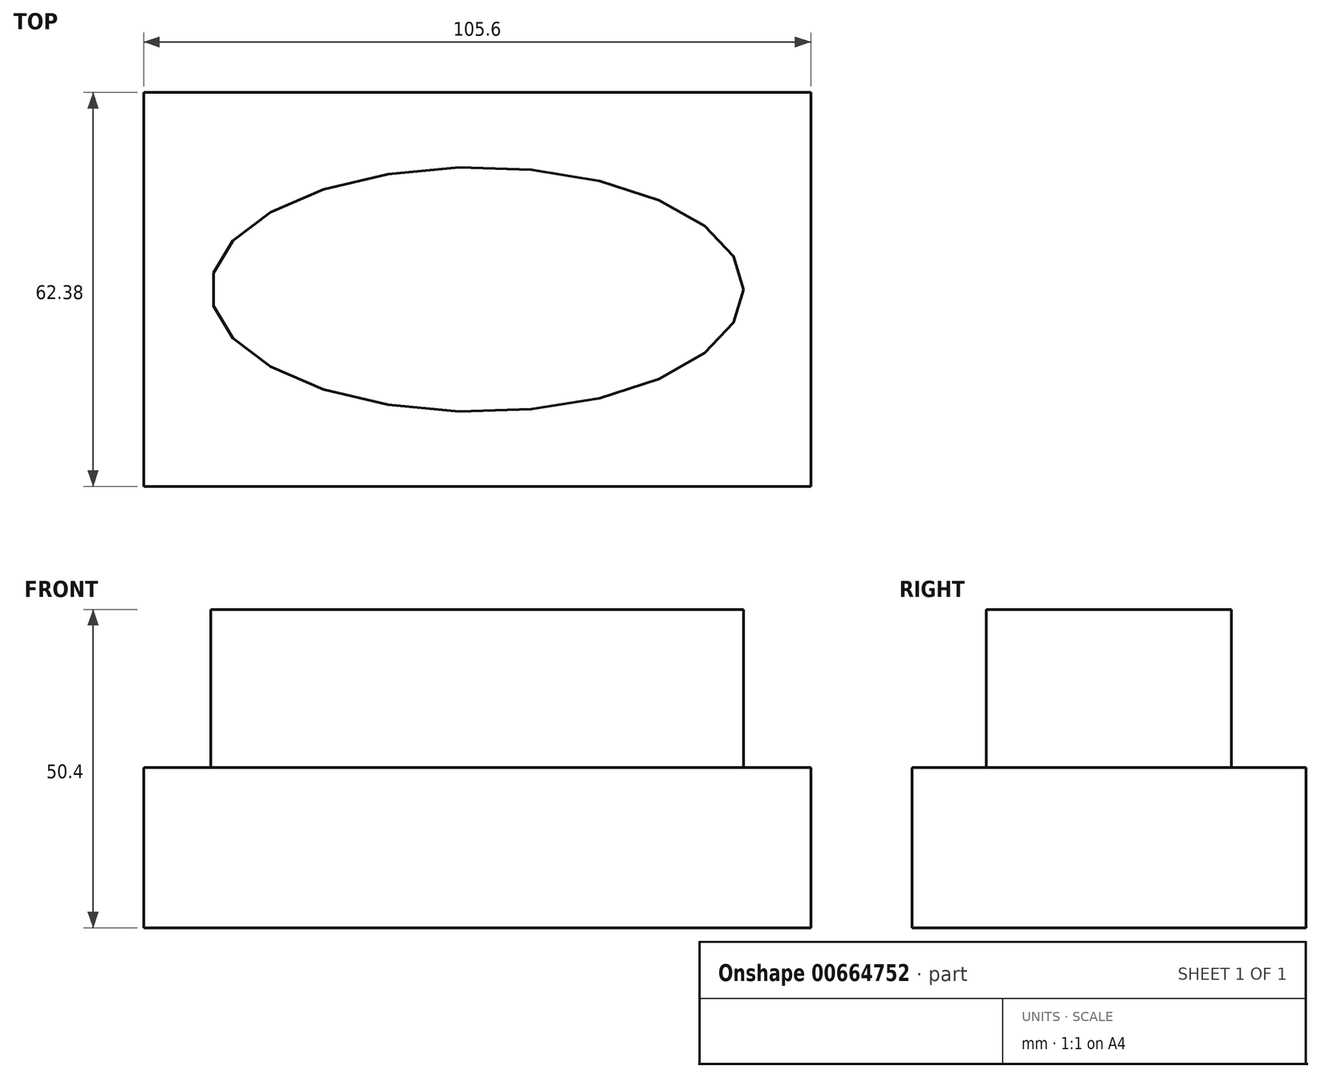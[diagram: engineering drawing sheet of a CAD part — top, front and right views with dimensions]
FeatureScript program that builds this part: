
annotation { "Feature Type Name" : "Feature", "Feature Type Description" : "" }
export const myFeature = defineFeature(function(context is Context, id is Id, definition is map)
    precondition{}
    {
        {
            var Q0;
            Q0=qCreatedBy(makeId("Top.planeOp"),FACE);
            var sketch = newSketch(context, id + "F0", { "sketchPlane" : qUnion([Q0])});
            skLineSegment(sketch, "E0.bottom", {"start": v(52.8, 31.19) * mm, "end": v(-52.8, 31.19) * mm});
            skLineSegment(sketch, "E0.top", {"start": v(52.8, -31.19) * mm, "end": v(-52.8, -31.19) * mm});
            skLineSegment(sketch, "E0.left", {"start": v(52.8, 31.19) * mm, "end": v(52.8, -31.19) * mm});
            skLineSegment(sketch, "E0.right", {"start": v(-52.8, 31.19) * mm, "end": v(-52.8, -31.19) * mm});
            skPoint(sketch, "E0.middle", {"position": v(0, 0) * mm});
            skSolve(sketch);
        }
        {
            var Q0;
            Q0=makeQuery(id+"F0.imprint","IMPRINT",FACE,{"disambiguationData":[TD([[makeQuery(id+"F0.imprint","IMPRINT",EDGE,{"derivedFrom":sQuery(id+"F0.wireOp",EDGE,"E0.bottom")}),1.0]])]});
            extrude(context, id + "F1", {"entities" : qUnion([Q0]), "depth" : 25.4 * mm, "offsetDistance" : 25.4 * mm});
        }
        {
            var Q0;
            Q0=makeQuery(id+"F1.opExtrude","CAP_FACE",FACE,{"disambiguationData":[OSD([sQuery(id+"F0.wireOp",EDGE,"E0.bottom"),sQuery(id+"F0.wireOp",EDGE,"E0.top"),sQuery(id+"F0.wireOp",EDGE,"E0.left"),sQuery(id+"F0.wireOp",EDGE,"E0.right")])],"isStart":false});
            var sketch = newSketch(context, id + "F2", { "sketchPlane" : qUnion([Q0])});
            skEllipse(sketch, "E1", {"center": v(0, 0) * mm, "majorRadius": 42.15 * mm, "minorRadius": 19.38 * mm, "majorAxis": v(1, 0)});
            skSolve(sketch);
        }
        {
            var Q0;
            Q0=makeQuery(id+"F2.imprint","IMPRINT",FACE,{"disambiguationData":[TD([[makeQuery(id+"F2.imprint","IMPRINT",EDGE,{"derivedFrom":sQuery(id+"F2.wireOp",EDGE,"E1")}),1.0]])]});
            extrude(context, id + "F3", {"entities" : qUnion([Q0]), "operationType" : NewBodyOperationType.ADD, "depth" : 25 * mm, "offsetDistance" : 25 * mm});
        }
    });
